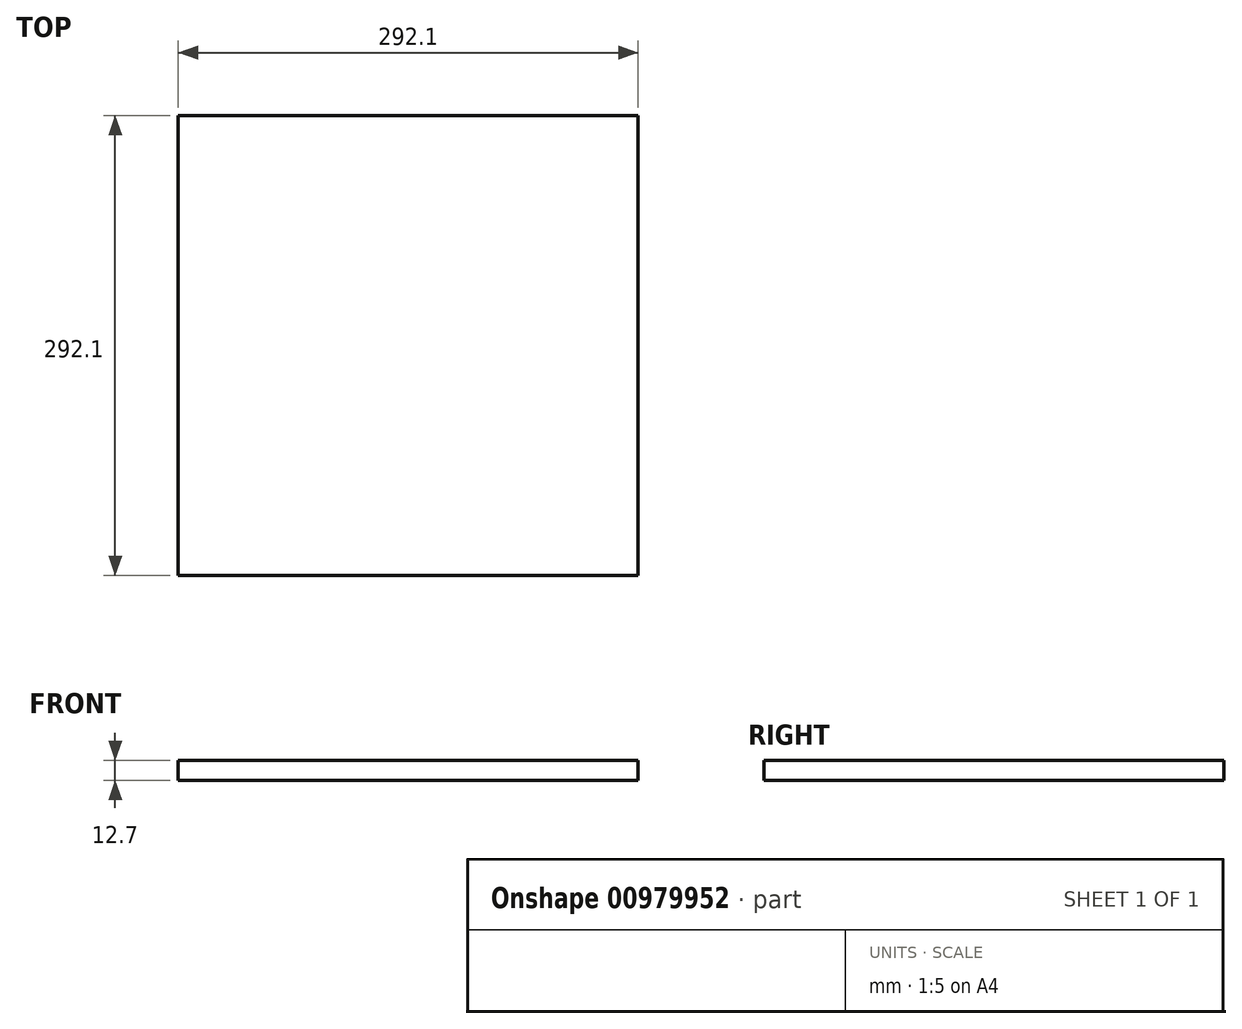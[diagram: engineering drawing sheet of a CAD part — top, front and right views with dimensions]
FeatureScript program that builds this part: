
annotation { "Feature Type Name" : "Feature", "Feature Type Description" : "" }
export const myFeature = defineFeature(function(context is Context, id is Id, definition is map)
    precondition{}
    {
        {
            var Q0;
            Q0=qCreatedBy(makeId("Top.planeOp"),FACE);
            var sketch = newSketch(context, id + "F0", { "sketchPlane" : qUnion([Q0])});
            skLineSegment(sketch, "E0.bottom", {"start": v(-146.05, 146.05) * mm, "end": v(146.05, 146.05) * mm});
            skLineSegment(sketch, "E0.top", {"start": v(-146.05, -146.05) * mm, "end": v(146.05, -146.05) * mm});
            skLineSegment(sketch, "E0.left", {"start": v(-146.05, 146.05) * mm, "end": v(-146.05, -146.05) * mm});
            skLineSegment(sketch, "E0.right", {"start": v(146.05, 146.05) * mm, "end": v(146.05, -146.05) * mm});
            skSolve(sketch);
        }
        {
            var Q0;
            Q0=qSketchRegion(id+"F0",true);
            extrude(context, id + "F1", {"entities" : qUnion([Q0]), "oppositeDirection" : true, "depth" : 12.7 * mm, "offsetDistance" : 25.4 * mm});
        }
    });
